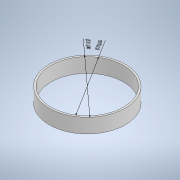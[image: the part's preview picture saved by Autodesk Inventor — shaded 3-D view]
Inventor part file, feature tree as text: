
AUTODESK INVENTOR PART (.ipt)
format: ipt  version: 2021 (Build 250183000, 183)  size: 115,200 bytes
history: native  units: mm
features: other x3, extrude x2, sketch x2
ambient origin geometry x8: Origin, YZ Plane, XZ Plane, XY Plane, X Axis, Y Axis, Z Axis, Center Point
bodies: Body1 (feature_tree)
feature tree (7):
  other  "Annotations"
  extrude  "Extrusion1"  Depth=21.0mm
  extrude  "Extrusion2"  Depth=4.0mm TaperAngle=0.0deg
  sketch  "Esquisse1"
  sketch  "Esquisse3"
  other  "Cote de diamètre 1"
  other  "Cote de diamètre 2"
